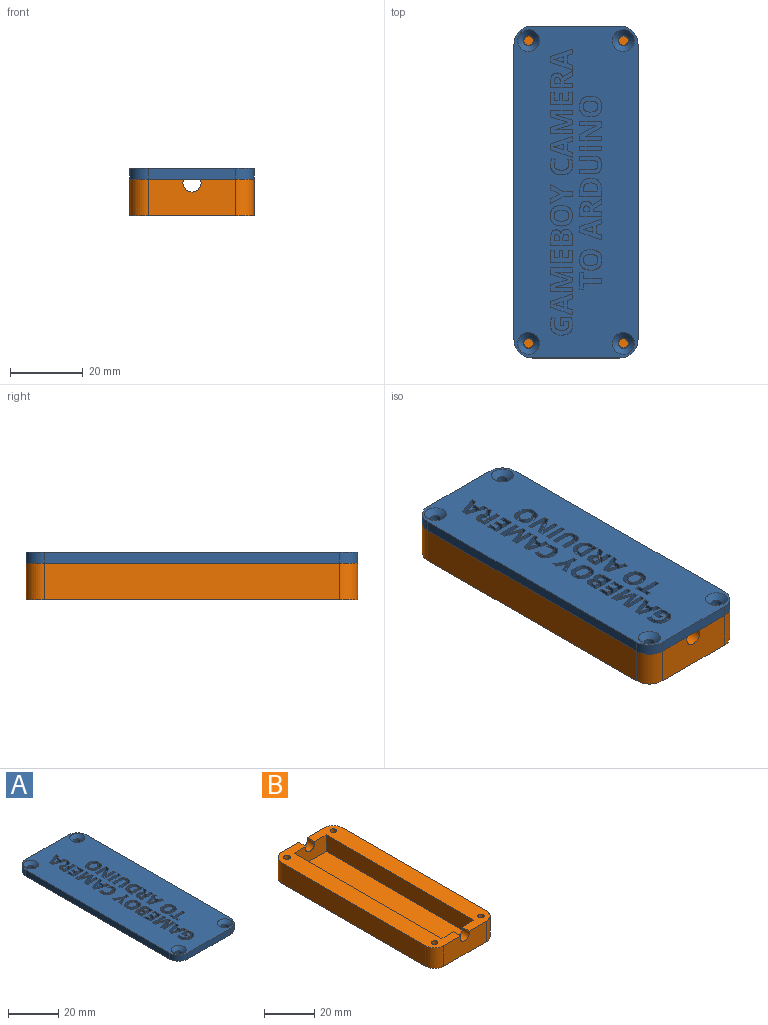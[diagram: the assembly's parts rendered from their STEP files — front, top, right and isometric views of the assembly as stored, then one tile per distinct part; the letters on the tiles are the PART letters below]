
ASSEMBLY  parts=2 mates=1
PART A: 363 faces, bbox 34x91x3 mm
  f0: plane 91x34mm, normal (0,0,1), area 2539.2mm2, adj f1,f2,f3,f8,f10,f11,f12,f13
  f1: plane 24x3mm, normal (0,1,0), area 72mm2, adj f0,f9,f14,f17
  f2: plane 81x3mm, normal (-1,0,0), area 243mm2, adj f0,f9,f14,f15
  f3: plane 24x3mm, normal (0,-1,0), area 72mm2, adj f0,f9,f15,f16
  f4: cylinder r=1.5mm len=3mm, axis (0,0,-1), area 14.1mm2, adj f9,f10
  f5: cylinder r=1.5mm len=3mm, axis (0,0,-1), area 14.1mm2, adj f9,f11
  f6: cylinder r=1.5mm len=3mm, axis (0,0,-1), area 14.1mm2, adj f9,f12
  f7: cylinder r=1.5mm len=3mm, axis (0,0,-1), area 14.1mm2, adj f9,f13
  f8: plane 81x3mm, normal (1,0,0), area 243mm2, adj f0,f9,f16,f17
  f9: plane 91x34mm, normal (0,0,-1), area 3044.3mm2, adj f1,f2,f3,f4,f5,f6,f7,f8
  f10: cone r=1.5mm half-angle=45deg, axis (0,0,1), area 30mm2, adj f0,f4
  f11: cone r=1.5mm half-angle=45deg, axis (0,0,1), area 30mm2, adj f0,f5
  f12: cone r=1.5mm half-angle=45deg, axis (0,0,1), area 30mm2, adj f0,f6
  f13: cone r=1.5mm half-angle=45deg, axis (0,0,1), area 30mm2, adj f0,f7
  f14: cylinder r=5mm len=5mm, axis (0,0,1), area 23.6mm2, adj f0,f1,f2,f9
  f15: cylinder r=5mm len=5mm, axis (0,0,-1), area 23.6mm2, adj f0,f2,f3,f9
  f16: cylinder r=5mm len=5mm, axis (0,0,1), area 23.6mm2, adj f0,f3,f8,f9
  f17: cylinder r=5mm len=5mm, axis (0,0,-1), area 23.6mm2, adj f0,f1,f8,f9
  f18: plane 4.66x2mm, normal (-0.31,-0.95,0), area 9.8mm2, adj f0,f19,f36,f37
  f19: plane 2x0.04mm, normal (-1,0,0), area 0.1mm2, adj f0,f18,f20,f37
  f20: extruded ~2x1.38mm, area 2.8mm2, adj f0,f19,f21,f37
  f21: extruded ~2x0.46mm, area 0.9mm2, adj f0,f20,f22,f37
  f22: plane 2.82x2mm, normal (0,1,0), area 5.6mm2, adj f0,f21,f23,f37
  f23: plane 2x1.18mm, normal (-1,0,0), area 2.4mm2, adj f0,f22,f24,f37
  f24: plane 5.95x2mm, normal (0,-1,0), area 11.9mm2, adj f0,f23,f25,f37
  f25: plane 2x1.72mm, normal (1,0,0), area 3.4mm2, adj f0,f24,f26,f37
  f26: plane 4.55x2mm, normal (0.31,0.95,0), area 9.6mm2, adj f0,f25,f27,f37
  f27: plane 2x0.02mm, normal (1,0,0), area 0mm2, adj f0,f26,f28,f37
  f28: plane 4.55x2mm, normal (0.3,-0.96,0), area 9.5mm2, adj f0,f27,f29,f37
  f29: plane 2x1.72mm, normal (1,0,0), area 3.4mm2, adj f0,f28,f30,f37
  f30: plane 5.95x2mm, normal (0,1,0), area 11.9mm2, adj f0,f29,f31,f37
  f31: plane 2x1.13mm, normal (-1,0,0), area 2.3mm2, adj f0,f30,f32,f37
  f32: plane 2.77x2mm, normal (0,-1,0), area 5.5mm2, adj f0,f31,f33,f37
  f33: extruded ~2x1.9mm, area 3.8mm2, adj f0,f32,f34,f37
  f34: plane 2x0.04mm, normal (-1,0,0), area 0.1mm2, adj f0,f33,f35,f37
  f35: plane 4.67x2mm, normal (-0.29,0.96,0), area 9.8mm2, adj f0,f34,f36,f37
  f36: plane 2x1.16mm, normal (-1,0,0), area 2.3mm2, adj f0,f18,f35,f37
  f37: plane 6.36x5.95mm, normal (0,0,1), area 24.4mm2, adj f18,f19,f20,f21,f22,f23,f24,f25
  f38: plane 2x1.13mm, normal (-1,0,0), area 2.3mm2, adj f0,f39,f56,f57
  f39: plane 2x1.24mm, normal (0,1,0), area 2.5mm2, adj f0,f38,f40,f57
  f40: extruded ~2x0.8mm, area 1.6mm2, adj f0,f39,f41,f57
  f41: extruded ~2x1.15mm, area 2.6mm2, adj f0,f40,f42,f57
  f42: extruded ~2x1.48mm, area 3.1mm2, adj f0,f41,f43,f57
  f43: extruded ~2x1.48mm, area 3.2mm2, adj f0,f42,f44,f57
  f44: extruded ~2x1.31mm, area 2.9mm2, adj f0,f43,f45,f57
  f45: extruded ~2x1.36mm, area 2.8mm2, adj f0,f44,f46,f57
  f46: plane 2x1.01mm, normal (-0.38,-0.92,0), area 2.2mm2, adj f0,f45,f47,f57
  f47: extruded ~2x1.77mm, area 3.6mm2, adj f0,f46,f48,f57
  f48: extruded ~2.28x2mm, area 5mm2, adj f0,f47,f49,f57
  f49: extruded ~2.25x2mm, area 4.9mm2, adj f0,f48,f50,f57
  f50: extruded ~2.27x2mm, area 4.9mm2, adj f0,f49,f51,f57
  f51: extruded ~2.06x2mm, area 4.5mm2, adj f0,f50,f52,f57
  f52: extruded ~2x1.04mm, area 2.1mm2, adj f0,f51,f53,f57
  f53: extruded ~2x1.08mm, area 2.2mm2, adj f0,f52,f54,f57
  f54: plane 3.08x2mm, normal (0,-1,0), area 6.2mm2, adj f0,f53,f55,f57
  f55: plane 2.36x2mm, normal (1,0,0), area 4.7mm2, adj f0,f54,f56,f57
  f56: plane 2x1.05mm, normal (0,1,0), area 2.1mm2, adj f0,f38,f55,f57
  f57: plane 6.12x4.88mm, normal (0,0,1), area 17.2mm2, adj f38,f39,f40,f41,f42,f43,f44,f45
  f58: plane 2.28x2mm, normal (-0.53,0.85,0), area 5.4mm2, adj f0,f59,f75,f77
  f59: plane 2x1.4mm, normal (-1,0,0), area 2.8mm2, adj f0,f58,f60,f77
  f60: extruded ~2.59x2mm, area 6.3mm2, adj f0,f59,f61,f77
  f61: extruded ~2x0.82mm, area 2.1mm2, adj f0,f60,f62,f77
  f62: extruded ~2x0.93mm, area 2mm2, adj f0,f61,f63,f77
  f63: extruded ~2x1.34mm, area 3mm2, adj f0,f62,f64,f77
  f64: extruded ~2x1.8mm, area 3.8mm2, adj f0,f63,f65,f77
  f65: plane 2x1.73mm, normal (1,0,0), area 3.5mm2, adj f0,f64,f66,f77
  f66: plane 5.95x2mm, normal (0,1,0), area 11.9mm2, adj f0,f65,f67,f77
  f67: plane 2x1.26mm, normal (-1,0,0), area 2.5mm2, adj f0,f66,f68,f77
  f68: plane 2.28x2mm, normal (0,-1,0), area 4.6mm2, adj f0,f67,f75,f77
  f69: plane 2x0.38mm, normal (-1,0,0), area 0.8mm2, adj f70,f76,f77,f361
  f70: extruded ~2x0.9mm, area 1.9mm2, adj f69,f71,f77,f361
  f71: extruded ~2x0.6mm, area 1.4mm2, adj f70,f72,f77,f361
  f72: extruded ~2x0.63mm, area 1.4mm2, adj f71,f73,f77,f361
  f73: extruded ~2x0.88mm, area 1.8mm2, adj f72,f74,f77,f361
  f74: plane 2x0.41mm, normal (1,0,0), area 0.8mm2, adj f73,f76,f77,f361
  f75: plane 2x0.67mm, normal (-1,0,0), area 1.3mm2, adj f0,f58,f68,f77
  f76: plane 2x1.61mm, normal (0,-1,0), area 3.2mm2, adj f69,f74,f77,f361
  f77: plane 5.95x4.75mm, normal (0,0,1), area 17.3mm2, adj f58,f59,f60,f61,f62,f63,f64,f65
  f78: plane 2x0.54mm, normal (1,0,0), area 1.1mm2, adj f79,f88,f90,f91
  f79: plane 3.87x2mm, normal (0,-1,0), area 7.7mm2, adj f78,f80,f90,f91
  f80: plane 2x0.67mm, normal (-1,0,0), area 1.3mm2, adj f79,f81,f90,f91
  f81: extruded ~2x1.92mm, area 5.9mm2, adj f80,f88,f90,f91
  f82: extruded ~2.26x2mm, area 4.9mm2, adj f0,f83,f89,f90
  f83: plane 2x1.87mm, normal (1,0,0), area 3.7mm2, adj f0,f82,f84,f90
  f84: plane 5.95x2mm, normal (0,1,0), area 11.9mm2, adj f0,f83,f85,f90
  f85: plane 2x1.69mm, normal (-1,0,0), area 3.4mm2, adj f0,f84,f86,f90
  f86: extruded ~2.41x2mm, area 5.2mm2, adj f0,f85,f87,f90
  f87: extruded ~2.25x2mm, area 4.9mm2, adj f0,f86,f89,f90
  f88: extruded ~2x1.96mm, area 6.1mm2, adj f78,f81,f90,f91
  f89: extruded ~2.15x2mm, area 4.7mm2, adj f0,f82,f87,f90
  f90: plane 5.95x4.94mm, normal (0,0,1), area 18mm2, adj f78,f79,f80,f81,f82,f83,f84,f85
  f91: plane 3.87x2.36mm, normal (0,0,1), area 8mm2, adj f78,f79,f80,f81,f88
  f92: extruded ~2x1.13mm, area 2.6mm2, adj f93,f104,f106,f107
  f93: extruded ~2.01x2mm, area 5.7mm2, adj f92,f94,f106,f107
  f94: extruded ~2.01x2mm, area 5.7mm2, adj f93,f95,f106,f107
  f95: extruded ~2x1.13mm, area 2.6mm2, adj f94,f96,f106,f107
  f96: extruded ~2x1.5mm, area 3.1mm2, adj f95,f104,f106,f107
  f97: extruded ~2.1x2mm, area 4.6mm2, adj f0,f98,f105,f106
  f98: extruded ~2.11x2mm, area 4.6mm2, adj f0,f97,f99,f106
  f99: extruded ~2.27x2mm, area 4.9mm2, adj f0,f98,f100,f106
  f100: extruded ~2.28x2mm, area 4.9mm2, adj f0,f99,f101,f106
  f101: extruded ~2.1x2mm, area 4.6mm2, adj f0,f100,f102,f106
  f102: extruded ~2.1x2mm, area 4.6mm2, adj f0,f101,f103,f106
  f103: extruded ~2.27x2mm, area 4.9mm2, adj f0,f102,f105,f106
  f104: extruded ~2x1.5mm, area 3.2mm2, adj f92,f96,f106,f107
  f105: extruded ~2.27x2mm, area 4.9mm2, adj f0,f97,f103,f106
  f106: plane 6.13x5.66mm, normal (0,0,1), area 18.5mm2, adj f92,f93,f94,f95,f96,f97,f98,f99
  f107: plane 4.02x3.02mm, normal (0,0,1), area 10.1mm2, adj f92,f93,f94,f95,f96,f104
  f108: extruded ~2x1.06mm, area 2.9mm2, adj f109,f130,f133,f135
  f109: extruded ~2x0.61mm, area 1.4mm2, adj f108,f110,f133,f135
  f110: extruded ~2x0.77mm, area 1.6mm2, adj f109,f111,f133,f135
  f111: plane 2x0.82mm, normal (1,0,0), area 1.6mm2, adj f110,f112,f133,f135
  f112: plane 2x1.55mm, normal (0,-1,0), area 3.1mm2, adj f111,f130,f133,f135
  f113: plane 2x0.66mm, normal (-1,0,0), area 1.3mm2, adj f114,f131,f133,f134
  f114: extruded ~2x0.79mm, area 1.6mm2, adj f113,f115,f133,f134
  f115: extruded ~2x0.49mm, area 1.2mm2, adj f114,f116,f133,f134
  f116: extruded ~2x0.52mm, area 1.2mm2, adj f115,f117,f133,f134
  f117: extruded ~2x0.74mm, area 1.5mm2, adj f116,f118,f133,f134
  f118: plane 2x0.73mm, normal (1,0,0), area 1.5mm2, adj f117,f131,f133,f134
  f119: plane 2.23x2mm, normal (-1,0,0), area 4.5mm2, adj f0,f120,f132,f133
  f120: extruded ~2x1.6mm, area 3.4mm2, adj f0,f119,f121,f133
  f121: extruded ~2x1.27mm, area 2.9mm2, adj f0,f120,f122,f133
  f122: extruded ~2x0.92mm, area 1.9mm2, adj f0,f121,f123,f133
  f123: extruded ~2x0.82mm, area 1.9mm2, adj f0,f122,f124,f133
  f124: plane 2x0.04mm, normal (0,-1,0), area 0.1mm2, adj f0,f123,f125,f133
  f125: extruded ~2x0.67mm, area 1.6mm2, adj f0,f124,f126,f133
  f126: extruded ~2x0.88mm, area 1.9mm2, adj f0,f125,f127,f133
  f127: extruded ~2x1.15mm, area 2.7mm2, adj f0,f126,f128,f133
  f128: extruded ~2x1.84mm, area 3.8mm2, adj f0,f127,f129,f133
  f129: plane 2x1.85mm, normal (1,0,0), area 3.7mm2, adj f0,f128,f132,f133
  f130: plane 2x0.78mm, normal (-1,0,0), area 1.6mm2, adj f108,f112,f133,f135
  f131: plane 2x1.32mm, normal (0,-1,0), area 2.6mm2, adj f113,f118,f133,f134
  f132: plane 5.95x2mm, normal (0,1,0), area 11.9mm2, adj f0,f119,f129,f133
  f133: plane 5.95x4.41mm, normal (0,0,1), area 19.3mm2, adj f108,f109,f110,f111,f112,f113,f114,f115
  f134: plane 1.7x1.32mm, normal (0,0,1), area 2.1mm2, adj f113,f114,f115,f116,f117,f118,f131
  f135: plane 1.84x1.55mm, normal (0,0,1), area 2.6mm2, adj f108,f109,f110,f111,f112,f130
  f136: plane 2.16x2mm, normal (1,0,0), area 4.3mm2, adj f0,f137,f147,f148
  f137: plane 2x1.53mm, normal (0,-1,0), area 3.1mm2, adj f0,f136,f138,f148
  f138: plane 2.01x2mm, normal (-1,0,0), area 4mm2, adj f0,f137,f139,f148
  f139: plane 2x1.03mm, normal (0,-1,0), area 2.1mm2, adj f0,f138,f140,f148
  f140: plane 2.01x2mm, normal (1,0,0), area 4mm2, adj f0,f139,f141,f148
  f141: plane 2x1.31mm, normal (0,-1,0), area 2.6mm2, adj f0,f140,f142,f148
  f142: plane 2.16x2mm, normal (-1,0,0), area 4.3mm2, adj f0,f141,f143,f148
  f143: plane 2x1.03mm, normal (0,-1,0), area 2.1mm2, adj f0,f142,f144,f148
  f144: plane 3.43x2mm, normal (1,0,0), area 6.9mm2, adj f0,f143,f145,f148
  f145: plane 5.95x2mm, normal (0,1,0), area 11.9mm2, adj f0,f144,f146,f148
  f146: plane 3.43x2mm, normal (-1,0,0), area 6.9mm2, adj f0,f145,f147,f148
  f147: plane 2x1.04mm, normal (0,-1,0), area 2.1mm2, adj f0,f136,f146,f148
  f148: plane 5.95x3.43mm, normal (0,0,1), area 14.1mm2, adj f136,f137,f138,f139,f140,f141,f142,f143
  f149: plane 2x1.61mm, normal (-1,0,0), area 3.2mm2, adj f0,f150,f156,f157
  f150: plane 2x1.05mm, normal (0,-1,0), area 2.1mm2, adj f0,f149,f151,f157
  f151: plane 4.49x2mm, normal (1,0,0), area 9mm2, adj f0,f150,f152,f157
  f152: plane 2x1.05mm, normal (0,1,0), area 2.1mm2, adj f0,f151,f153,f157
  f153: plane 2x1.62mm, normal (-1,0,0), area 3.2mm2, adj f0,f152,f154,f157
  f154: plane 4.9x2mm, normal (0,1,0), area 9.8mm2, adj f0,f153,f155,f157
  f155: plane 2x1.26mm, normal (-1,0,0), area 2.5mm2, adj f0,f154,f156,f157
  f156: plane 4.9x2mm, normal (0,-1,0), area 9.8mm2, adj f0,f149,f155,f157
  f157: plane 5.95x4.49mm, normal (0,0,1), area 10.9mm2, adj f149,f150,f151,f152,f153,f154,f155,f156
  f158: plane 3.63x2mm, normal (0,1,0), area 7.3mm2, adj f0,f159,f172,f173
  f159: extruded ~2x1.02mm, area 2.1mm2, adj f0,f158,f160,f173
  f160: extruded ~2x0.9mm, area 2mm2, adj f0,f159,f161,f173
  f161: extruded ~2x0.92mm, area 2mm2, adj f0,f160,f162,f173
  f162: extruded ~2x1.01mm, area 2.1mm2, adj f0,f161,f163,f173
  f163: plane 3.64x2mm, normal (0,-1,0), area 7.3mm2, adj f0,f162,f164,f173
  f164: plane 2x1.26mm, normal (1,0,0), area 2.5mm2, adj f0,f163,f165,f173
  f165: plane 3.83x2mm, normal (0,1,0), area 7.7mm2, adj f0,f164,f166,f173
  f166: extruded ~2x1.61mm, area 3.6mm2, adj f0,f165,f167,f173
  f167: extruded ~2x1.78mm, area 3.8mm2, adj f0,f166,f168,f173
  f168: extruded ~2x1.32mm, area 2.7mm2, adj f0,f167,f169,f173
  f169: extruded ~2x0.85mm, area 2.3mm2, adj f0,f168,f170,f173
  f170: extruded ~2x1.16mm, area 2.4mm2, adj f0,f169,f171,f173
  f171: plane 3.85x2mm, normal (0,-1,0), area 7.7mm2, adj f0,f170,f172,f173
  f172: plane 2x1.26mm, normal (1,0,0), area 2.5mm2, adj f0,f158,f171,f173
  f173: plane 6.03x4.88mm, normal (0,0,1), area 16.2mm2, adj f158,f159,f160,f161,f162,f163,f164,f165
  f174: plane 5.95x2mm, normal (0,-1,0), area 11.9mm2, adj f0,f175,f177,f178
  f175: plane 2x1.26mm, normal (1,0,0), area 2.5mm2, adj f0,f174,f176,f178
  f176: plane 5.95x2mm, normal (0,1,0), area 11.9mm2, adj f0,f175,f177,f178
  f177: plane 2x1.26mm, normal (-1,0,0), area 2.5mm2, adj f0,f174,f176,f178
  f178: plane 5.95x1.26mm, normal (0,0,1), area 7.5mm2, adj f174,f175,f176,f177
  f179: plane 4.66x2mm, normal (-0.31,-0.95,0), area 9.8mm2, adj f0,f180,f197,f198
  f180: plane 2x0.04mm, normal (-1,0,0), area 0.1mm2, adj f0,f179,f181,f198
  f181: extruded ~2x1.38mm, area 2.8mm2, adj f0,f180,f182,f198
  f182: extruded ~2x0.46mm, area 0.9mm2, adj f0,f181,f183,f198
  f183: plane 2.82x2mm, normal (0,1,0), area 5.6mm2, adj f0,f182,f184,f198
  f184: plane 2x1.18mm, normal (-1,0,0), area 2.4mm2, adj f0,f183,f185,f198
  f185: plane 5.95x2mm, normal (0,-1,0), area 11.9mm2, adj f0,f184,f186,f198
  f186: plane 2x1.72mm, normal (1,0,0), area 3.4mm2, adj f0,f185,f187,f198
  f187: plane 4.55x2mm, normal (0.31,0.95,0), area 9.6mm2, adj f0,f186,f188,f198
  f188: plane 2x0.02mm, normal (1,0,0), area 0mm2, adj f0,f187,f189,f198
  f189: plane 4.55x2mm, normal (0.3,-0.96,0), area 9.5mm2, adj f0,f188,f190,f198
  f190: plane 2x1.72mm, normal (1,0,0), area 3.4mm2, adj f0,f189,f191,f198
  f191: plane 5.95x2mm, normal (0,1,0), area 11.9mm2, adj f0,f190,f192,f198
  f192: plane 2x1.13mm, normal (-1,0,0), area 2.3mm2, adj f0,f191,f193,f198
  f193: plane 2.77x2mm, normal (0,-1,0), area 5.5mm2, adj f0,f192,f194,f198
  f194: extruded ~2x1.9mm, area 3.8mm2, adj f0,f193,f195,f198
  f195: plane 2x0.04mm, normal (-1,0,0), area 0.1mm2, adj f0,f194,f196,f198
  f196: plane 4.67x2mm, normal (-0.29,0.96,0), area 9.8mm2, adj f0,f195,f197,f198
  f197: plane 2x1.16mm, normal (-1,0,0), area 2.3mm2, adj f0,f179,f196,f198
  f198: plane 6.36x5.95mm, normal (0,0,1), area 24.4mm2, adj f179,f180,f181,f182,f183,f184,f185,f186
  f199: extruded ~2x0.67mm, area 1.5mm2, adj f0,f200,f213,f214
  f200: plane 2x1.03mm, normal (-0.37,-0.93,0), area 2.2mm2, adj f0,f199,f201,f214
  f201: extruded ~2x1.74mm, area 3.6mm2, adj f0,f200,f202,f214
  f202: extruded ~2x1.48mm, area 3.1mm2, adj f0,f201,f203,f214
  f203: extruded ~2x1.07mm, area 2.9mm2, adj f0,f202,f204,f214
  f204: extruded ~2x1.63mm, area 3.4mm2, adj f0,f203,f205,f214
  f205: extruded ~2.26x2mm, area 4.8mm2, adj f0,f204,f206,f214
  f206: extruded ~2x1.99mm, area 4.4mm2, adj f0,f205,f207,f214
  f207: extruded ~2x1.64mm, area 3.3mm2, adj f0,f206,f208,f214
  f208: plane 2x1.06mm, normal (0,-1,0), area 2.1mm2, adj f0,f207,f209,f214
  f209: extruded ~2x1.52mm, area 3.1mm2, adj f0,f208,f210,f214
  f210: extruded ~2x1.99mm, area 5.7mm2, adj f0,f209,f211,f214
  f211: extruded ~2x1.49mm, area 3.1mm2, adj f0,f210,f212,f214
  f212: extruded ~2x1.1mm, area 2.6mm2, adj f0,f211,f213,f214
  f213: extruded ~2x0.66mm, area 1.4mm2, adj f0,f199,f212,f214
  f214: plane 6.12x4.53mm, normal (0,0,1), area 12.4mm2, adj f199,f200,f201,f202,f203,f204,f205,f206
  f215: plane 2x1.37mm, normal (1,0,0), area 2.7mm2, adj f0,f216,f223,f224
  f216: plane 3.67x2mm, normal (-0.47,0.88,0), area 8.3mm2, adj f0,f215,f217,f224
  f217: plane 2.27x2mm, normal (0,1,0), area 4.5mm2, adj f0,f216,f218,f224
  f218: plane 2x1.25mm, normal (-1,0,0), area 2.5mm2, adj f0,f217,f219,f224
  f219: plane 2.32x2mm, normal (0,-1,0), area 4.6mm2, adj f0,f218,f220,f224
  f220: plane 3.63x2mm, normal (-0.48,-0.88,0), area 8.3mm2, adj f0,f219,f221,f224
  f221: plane 2x1.36mm, normal (1,0,0), area 2.7mm2, adj f0,f220,f222,f224
  f222: plane 2.45x2mm, normal (0.45,0.89,0), area 5.5mm2, adj f0,f221,f223,f224
  f223: plane 2.45x2mm, normal (0.45,-0.89,0), area 5.5mm2, adj f0,f215,f222,f224
  f224: plane 5.95x5.2mm, normal (0,0,1), area 11.6mm2, adj f215,f216,f217,f218,f219,f220,f221,f222
  f225: plane 2.16x2mm, normal (1,0,0), area 4.3mm2, adj f0,f226,f236,f237
  f226: plane 2x1.53mm, normal (0,-1,0), area 3.1mm2, adj f0,f225,f227,f237
  f227: plane 2.01x2mm, normal (-1,0,0), area 4mm2, adj f0,f226,f228,f237
  f228: plane 2x1.03mm, normal (0,-1,0), area 2.1mm2, adj f0,f227,f229,f237
  f229: plane 2.01x2mm, normal (1,0,0), area 4mm2, adj f0,f228,f230,f237
  f230: plane 2x1.31mm, normal (0,-1,0), area 2.6mm2, adj f0,f229,f231,f237
  f231: plane 2.16x2mm, normal (-1,0,0), area 4.3mm2, adj f0,f230,f232,f237
  f232: plane 2x1.03mm, normal (0,-1,0), area 2.1mm2, adj f0,f231,f233,f237
  f233: plane 3.43x2mm, normal (1,0,0), area 6.9mm2, adj f0,f232,f234,f237
  f234: plane 5.95x2mm, normal (0,1,0), area 11.9mm2, adj f0,f233,f235,f237
  f235: plane 3.43x2mm, normal (-1,0,0), area 6.9mm2, adj f0,f234,f236,f237
  f236: plane 2x1.04mm, normal (0,-1,0), area 2.1mm2, adj f0,f225,f235,f237
  f237: plane 5.95x3.43mm, normal (0,0,1), area 14.1mm2, adj f225,f226,f227,f228,f229,f230,f231,f232
  f238: extruded ~2.58x2mm, area 5.4mm2, adj f239,f248,f250,f251
  f239: extruded ~2x0.4mm, area 0.8mm2, adj f238,f240,f250,f251
  f240: extruded ~2.18x2mm, area 4.6mm2, adj f239,f248,f250,f251
  f241: plane 5.97x2.11mm, normal (0.33,-0.94,0), area 12.7mm2, adj f0,f242,f249,f250
  f242: plane 2x1.54mm, normal (1,0,0), area 3.1mm2, adj f0,f241,f243,f250
  f243: plane 5.97x2.1mm, normal (0.33,0.94,0), area 12.7mm2, adj f0,f242,f244,f250
  f244: plane 2x1.36mm, normal (-1,0,0), area 2.7mm2, adj f0,f243,f245,f250
  f245: plane 2x1.42mm, normal (-0.29,-0.96,0), area 3mm2, adj f0,f244,f246,f250
  f246: plane 2.17x2mm, normal (-1,0,0), area 4.3mm2, adj f0,f245,f247,f250
  f247: plane 2x1.42mm, normal (-0.29,0.96,0), area 3mm2, adj f0,f246,f249,f250
  f248: plane 2x1.55mm, normal (1,0,0), area 3.1mm2, adj f238,f240,f250,f251
  f249: plane 2x1.36mm, normal (-1,0,0), area 2.7mm2, adj f0,f241,f247,f250
  f250: plane 5.97x5.75mm, normal (0,0,1), area 16.1mm2, adj f238,f239,f240,f241,f242,f243,f244,f245
  f251: plane 2.58x1.55mm, normal (0,0,1), area 2mm2, adj f238,f239,f240,f248
  f252: extruded ~2x1.13mm, area 2.6mm2, adj f253,f264,f266,f267
  f253: extruded ~2.01x2mm, area 5.7mm2, adj f252,f254,f266,f267
  f254: extruded ~2.01x2mm, area 5.7mm2, adj f253,f255,f266,f267
  f255: extruded ~2x1.13mm, area 2.6mm2, adj f254,f256,f266,f267
  f256: extruded ~2x1.5mm, area 3.1mm2, adj f255,f264,f266,f267
  f257: extruded ~2.1x2mm, area 4.6mm2, adj f0,f258,f265,f266
  f258: extruded ~2.11x2mm, area 4.6mm2, adj f0,f257,f259,f266
  f259: extruded ~2.27x2mm, area 4.9mm2, adj f0,f258,f260,f266
  f260: extruded ~2.28x2mm, area 4.9mm2, adj f0,f259,f261,f266
  f261: extruded ~2.1x2mm, area 4.6mm2, adj f0,f260,f262,f266
  f262: extruded ~2.1x2mm, area 4.6mm2, adj f0,f261,f263,f266
  f263: extruded ~2.27x2mm, area 4.9mm2, adj f0,f262,f265,f266
  f264: extruded ~2x1.5mm, area 3.2mm2, adj f252,f256,f266,f267
  f265: extruded ~2.27x2mm, area 4.9mm2, adj f0,f257,f263,f266
  f266: plane 6.13x5.66mm, normal (0,0,1), area 18.5mm2, adj f252,f253,f254,f255,f256,f257,f258,f259
  f267: plane 4.02x3.02mm, normal (0,0,1), area 10.1mm2, adj f252,f253,f254,f255,f256,f264
  f268: extruded ~2.58x2mm, area 5.4mm2, adj f269,f278,f280,f281
  f269: extruded ~2x0.4mm, area 0.8mm2, adj f268,f270,f280,f281
  f270: extruded ~2.18x2mm, area 4.6mm2, adj f269,f278,f280,f281
  f271: plane 5.97x2.11mm, normal (0.33,-0.94,0), area 12.7mm2, adj f0,f272,f279,f280
  f272: plane 2x1.54mm, normal (1,0,0), area 3.1mm2, adj f0,f271,f273,f280
  f273: plane 5.97x2.1mm, normal (0.33,0.94,0), area 12.7mm2, adj f0,f272,f274,f280
  f274: plane 2x1.36mm, normal (-1,0,0), area 2.7mm2, adj f0,f273,f275,f280
  f275: plane 2x1.42mm, normal (-0.29,-0.96,0), area 3mm2, adj f0,f274,f276,f280
  f276: plane 2.17x2mm, normal (-1,0,0), area 4.3mm2, adj f0,f275,f277,f280
  f277: plane 2x1.42mm, normal (-0.29,0.96,0), area 3mm2, adj f0,f276,f279,f280
  f278: plane 2x1.55mm, normal (1,0,0), area 3.1mm2, adj f268,f270,f280,f281
  f279: plane 2x1.36mm, normal (-1,0,0), area 2.7mm2, adj f0,f271,f277,f280
  f280: plane 5.97x5.75mm, normal (0,0,1), area 16.1mm2, adj f268,f269,f270,f271,f272,f273,f274,f275
  f281: plane 2.58x1.55mm, normal (0,0,1), area 2mm2, adj f268,f269,f270,f278
  f282: plane 2.28x2mm, normal (-0.53,0.85,0), area 5.4mm2, adj f0,f283,f299,f301
  f283: plane 2x1.4mm, normal (-1,0,0), area 2.8mm2, adj f0,f282,f284,f301
  f284: extruded ~2.59x2mm, area 6.3mm2, adj f0,f283,f285,f301
  f285: extruded ~2x0.82mm, area 2.1mm2, adj f0,f284,f286,f301
  f286: extruded ~2x0.93mm, area 2mm2, adj f0,f285,f287,f301
  f287: extruded ~2x1.34mm, area 3mm2, adj f0,f286,f288,f301
  f288: extruded ~2x1.8mm, area 3.8mm2, adj f0,f287,f289,f301
  f289: plane 2x1.73mm, normal (1,0,0), area 3.5mm2, adj f0,f288,f290,f301
  f290: plane 5.95x2mm, normal (0,1,0), area 11.9mm2, adj f0,f289,f291,f301
  f291: plane 2x1.26mm, normal (-1,0,0), area 2.5mm2, adj f0,f290,f292,f301
  f292: plane 2.28x2mm, normal (0,-1,0), area 4.6mm2, adj f0,f291,f299,f301
  f293: plane 2x0.38mm, normal (-1,0,0), area 0.8mm2, adj f294,f300,f301,f362
  f294: extruded ~2x0.9mm, area 1.9mm2, adj f293,f295,f301,f362
  f295: extruded ~2x0.6mm, area 1.4mm2, adj f294,f296,f301,f362
  f296: extruded ~2x0.63mm, area 1.4mm2, adj f295,f297,f301,f362
  f297: extruded ~2x0.88mm, area 1.8mm2, adj f296,f298,f301,f362
  f298: plane 2x0.41mm, normal (1,0,0), area 0.8mm2, adj f297,f300,f301,f362
  f299: plane 2x0.67mm, normal (-1,0,0), area 1.3mm2, adj f0,f282,f292,f301
  f300: plane 2x1.61mm, normal (0,-1,0), area 3.2mm2, adj f293,f298,f301,f362
  f301: plane 5.95x4.75mm, normal (0,0,1), area 17.3mm2, adj f282,f283,f284,f285,f286,f287,f288,f289
  f302: plane 2x1.14mm, normal (1,0,0), area 2.3mm2, adj f0,f303,f315,f316
  f303: plane 2.82x2mm, normal (0,1,0), area 5.6mm2, adj f0,f302,f304,f316
  f304: extruded ~2x1.64mm, area 3.3mm2, adj f0,f303,f305,f316
  f305: plane 2x0.03mm, normal (1,0,0), area 0.1mm2, adj f0,f304,f306,f316
  f306: plane 4.46x2.58mm, normal (0.5,-0.87,0), area 10.3mm2, adj f0,f305,f307,f316
  f307: plane 2x1.59mm, normal (1,0,0), area 3.2mm2, adj f0,f306,f308,f316
  f308: plane 5.95x2mm, normal (0,1,0), area 11.9mm2, adj f0,f307,f309,f316
  f309: plane 2x1.13mm, normal (-1,0,0), area 2.3mm2, adj f0,f308,f310,f316
  f310: plane 2.8x2mm, normal (0,-1,0), area 5.6mm2, adj f0,f309,f311,f316
  f311: extruded ~2x1.7mm, area 3.4mm2, adj f0,f310,f312,f316
  f312: plane 2x0.04mm, normal (-1,0,0), area 0.1mm2, adj f0,f311,f313,f316
  f313: plane 4.5x2.59mm, normal (-0.5,0.87,0), area 10.4mm2, adj f0,f312,f314,f316
  f314: plane 2x1.6mm, normal (-1,0,0), area 3.2mm2, adj f0,f313,f315,f316
  f315: plane 5.95x2mm, normal (0,-1,0), area 11.9mm2, adj f0,f302,f314,f316
  f316: plane 5.95x5.28mm, normal (0,0,1), area 20.1mm2, adj f302,f303,f304,f305,f306,f307,f308,f309
  f317: extruded ~2.58x2mm, area 5.4mm2, adj f318,f327,f329,f330
  f318: extruded ~2x0.4mm, area 0.8mm2, adj f317,f319,f329,f330
  f319: extruded ~2.18x2mm, area 4.6mm2, adj f318,f327,f329,f330
  f320: plane 5.97x2.11mm, normal (0.33,-0.94,0), area 12.7mm2, adj f0,f321,f328,f329
  f321: plane 2x1.54mm, normal (1,0,0), area 3.1mm2, adj f0,f320,f322,f329
  f322: plane 5.97x2.1mm, normal (0.33,0.94,0), area 12.7mm2, adj f0,f321,f323,f329
  f323: plane 2x1.36mm, normal (-1,0,0), area 2.7mm2, adj f0,f322,f324,f329
  f324: plane 2x1.42mm, normal (-0.29,-0.96,0), area 3mm2, adj f0,f323,f325,f329
  f325: plane 2.17x2mm, normal (-1,0,0), area 4.3mm2, adj f0,f324,f326,f329
  f326: plane 2x1.42mm, normal (-0.29,0.96,0), area 3mm2, adj f0,f325,f328,f329
  f327: plane 2x1.55mm, normal (1,0,0), area 3.1mm2, adj f317,f319,f329,f330
  f328: plane 2x1.36mm, normal (-1,0,0), area 2.7mm2, adj f0,f320,f326,f329
  f329: plane 5.97x5.75mm, normal (0,0,1), area 16.1mm2, adj f317,f318,f319,f320,f321,f322,f323,f324
  f330: plane 2.58x1.55mm, normal (0,0,1), area 2mm2, adj f317,f318,f319,f327
  f331: extruded ~2x1.13mm, area 2.6mm2, adj f332,f343,f345,f346
  f332: extruded ~2.01x2mm, area 5.7mm2, adj f331,f333,f345,f346
  f333: extruded ~2.01x2mm, area 5.7mm2, adj f332,f334,f345,f346
  f334: extruded ~2x1.13mm, area 2.6mm2, adj f333,f335,f345,f346
  f335: extruded ~2x1.5mm, area 3.1mm2, adj f334,f343,f345,f346
  f336: extruded ~2.1x2mm, area 4.6mm2, adj f0,f337,f344,f345
  f337: extruded ~2.11x2mm, area 4.6mm2, adj f0,f336,f338,f345
  f338: extruded ~2.27x2mm, area 4.9mm2, adj f0,f337,f339,f345
  f339: extruded ~2.28x2mm, area 4.9mm2, adj f0,f338,f340,f345
  f340: extruded ~2.1x2mm, area 4.6mm2, adj f0,f339,f341,f345
  f341: extruded ~2.1x2mm, area 4.6mm2, adj f0,f340,f342,f345
  f342: extruded ~2.27x2mm, area 4.9mm2, adj f0,f341,f344,f345
  f343: extruded ~2x1.5mm, area 3.2mm2, adj f331,f335,f345,f346
  f344: extruded ~2.27x2mm, area 4.9mm2, adj f0,f336,f342,f345
  f345: plane 6.13x5.66mm, normal (0,0,1), area 18.5mm2, adj f331,f332,f333,f334,f335,f336,f337,f338
  f346: plane 4.02x3.02mm, normal (0,0,1), area 10.1mm2, adj f331,f332,f333,f334,f335,f343
  f347: extruded ~2.58x2mm, area 5.4mm2, adj f348,f357,f359,f360
  f348: extruded ~2x0.4mm, area 0.8mm2, adj f347,f349,f359,f360
  f349: extruded ~2.18x2mm, area 4.6mm2, adj f348,f357,f359,f360
  f350: plane 5.97x2.11mm, normal (0.33,-0.94,0), area 12.7mm2, adj f0,f351,f358,f359
  f351: plane 2x1.54mm, normal (1,0,0), area 3.1mm2, adj f0,f350,f352,f359
  f352: plane 5.97x2.1mm, normal (0.33,0.94,0), area 12.7mm2, adj f0,f351,f353,f359
  f353: plane 2x1.36mm, normal (-1,0,0), area 2.7mm2, adj f0,f352,f354,f359
  f354: plane 2x1.42mm, normal (-0.29,-0.96,0), area 3mm2, adj f0,f353,f355,f359
  f355: plane 2.17x2mm, normal (-1,0,0), area 4.3mm2, adj f0,f354,f356,f359
  f356: plane 2x1.42mm, normal (-0.29,0.96,0), area 3mm2, adj f0,f355,f358,f359
  f357: plane 2x1.55mm, normal (1,0,0), area 3.1mm2, adj f347,f349,f359,f360
  f358: plane 2x1.36mm, normal (-1,0,0), area 2.7mm2, adj f0,f350,f356,f359
  f359: plane 5.97x5.75mm, normal (0,0,1), area 16.1mm2, adj f347,f348,f349,f350,f351,f352,f353,f354
  f360: plane 2.58x1.55mm, normal (0,0,1), area 2mm2, adj f347,f348,f349,f357
  f361: plane 1.61x1.57mm, normal (0,0,1), area 2.2mm2, adj f69,f70,f71,f72,f73,f74,f76
  f362: plane 1.61x1.57mm, normal (0,0,1), area 2.2mm2, adj f293,f294,f295,f296,f297,f298,f300
PART B: 26 faces, bbox 34x91x10 mm
  f0: plane 24x10mm, normal (0,-1,0), area 225.3mm2, adj f1,f5,f14,f21,f22,f25
  f1: plane 91x14.71mm, normal (0,0,1), area 760.3mm2, adj f0,f2,f3,f6,f8,f9,f12,f13
  f2: plane 24x10mm, normal (0,1,0), area 225.3mm2, adj f1,f5,f14,f20,f23,f24
  f3: plane 81x10mm, normal (-1,0,0), area 810mm2, adj f1,f5,f20,f21
  f4: plane 81x10mm, normal (1,0,0), area 810mm2, adj f5,f14,f22,f23
  f5: plane 91x34mm, normal (0,0,-1), area 3072.5mm2, adj f0,f2,f3,f4,f20,f21,f22,f23
  f6: plane 18x8mm, normal (0,-1,0), area 129.3mm2, adj f1,f7,f13,f14,f15,f24
  f7: plane 83x8mm, normal (-1,0,0), area 664mm2, adj f6,f8,f14,f15
  f8: plane 18x8mm, normal (0,1,0), area 129.3mm2, adj f1,f7,f13,f14,f15,f25
  f9: cylinder r=1.3mm len=8mm, axis (0,0,-1), area 65.3mm2, adj f1,f19
  f10: cylinder r=1.3mm len=8mm, axis (0,0,-1), area 65.3mm2, adj f14,f18
  f11: cylinder r=1.3mm len=8mm, axis (0,0,-1), area 65.3mm2, adj f14,f17
  f12: cylinder r=1.3mm len=8mm, axis (0,0,-1), area 65.3mm2, adj f1,f16
  f13: plane 83x8mm, normal (1,0,0), area 664mm2, adj f1,f6,f8,f15
  f14: plane 91x14.71mm, normal (0,0,1), area 760.3mm2, adj f0,f2,f4,f6,f7,f8,f10,f11
  f15: plane 83x18mm, normal (0,0,1), area 1494mm2, adj f6,f7,f8,f13
  f16: plane 2.6x2.6mm, normal (0,0,1), area 5.3mm2, adj f12
  f17: plane 2.6x2.6mm, normal (0,0,1), area 5.3mm2, adj f11
  f18: plane 2.6x2.6mm, normal (0,0,1), area 5.3mm2, adj f10
  f19: plane 2.6x2.6mm, normal (0,0,1), area 5.3mm2, adj f9
  f20: cylinder r=5mm len=10mm, axis (0,0,1), area 78.5mm2, adj f1,f2,f3,f5
  f21: cylinder r=5mm len=10mm, axis (0,0,-1), area 78.5mm2, adj f0,f1,f3,f5
  f22: cylinder r=5mm len=10mm, axis (0,0,1), area 78.5mm2, adj f0,f4,f5,f14
  f23: cylinder r=5mm len=10mm, axis (0,0,-1), area 78.5mm2, adj f2,f4,f5,f14
  f24: cylinder r=2.5mm len=5mm, axis (0,-1,0), area 39.6mm2, adj f1,f2,f6,f14
  f25: cylinder r=2.5mm len=5mm, axis (0,-1,0), area 39.6mm2, adj f0,f1,f8,f14
PLACE A t=(6.44,-8.33,-13.07)mm
PLACE B t=(6.44,-8.33,-23.07)mm
MATE cylindrical A.f7 <-> B.f12  axis (0,0,-1) through (-6.56,-49.83,-13.07)mm
